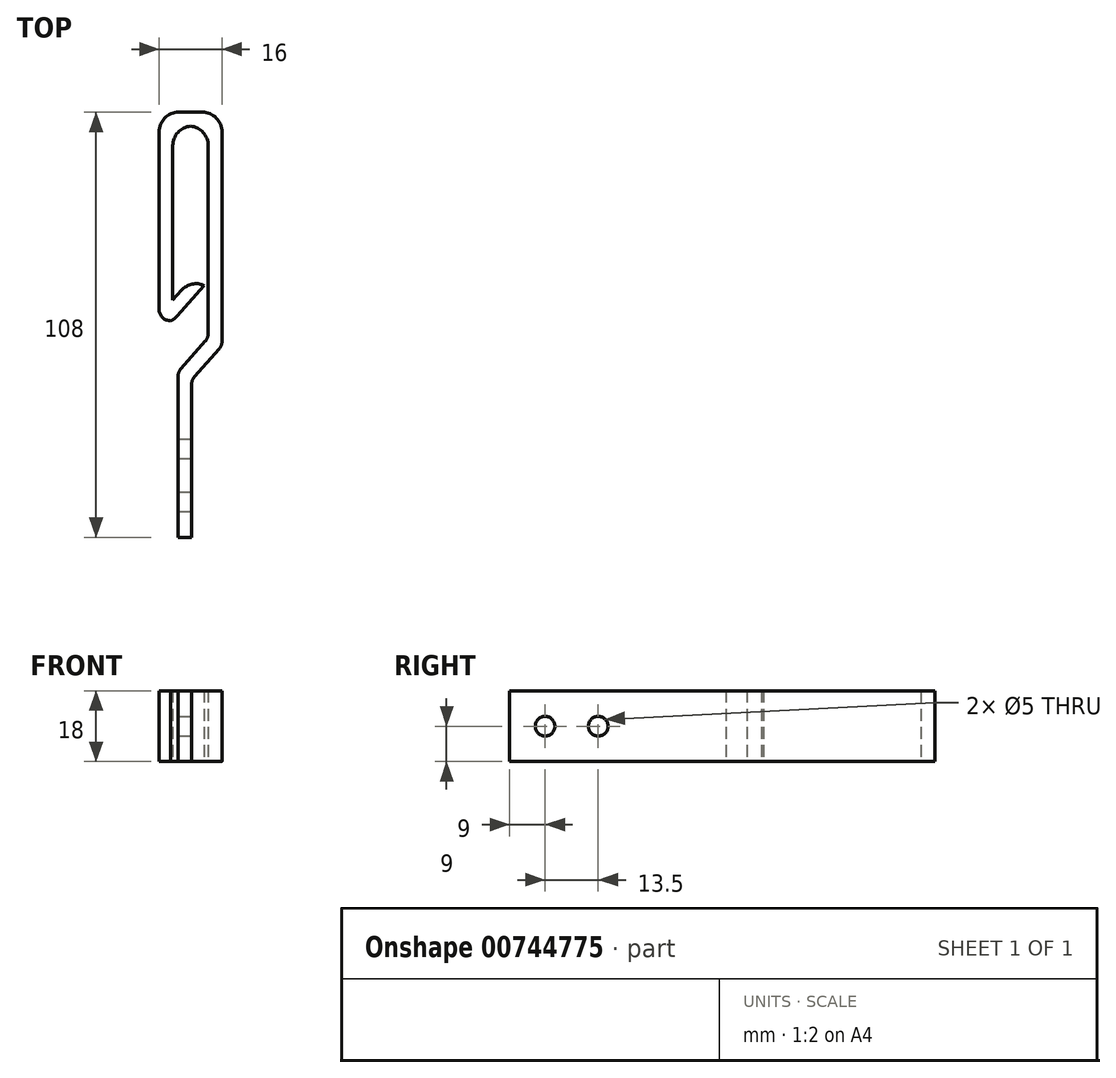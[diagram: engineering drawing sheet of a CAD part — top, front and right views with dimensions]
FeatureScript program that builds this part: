
annotation { "Feature Type Name" : "Feature", "Feature Type Description" : "" }
export const myFeature = defineFeature(function(context is Context, id is Id, definition is map)
    precondition{}
    {
        {
            var Q0;
            Q0=qCreatedBy(makeId("Top.planeOp"),FACE);
            var sketch = newSketch(context, id + "F0", { "sketchPlane" : qUnion([Q0])});
            skLineSegment(sketch, "E0.bottom", {"start": v(8, -54) * mm, "end": v(-8, -54) * mm});
            skLineSegment(sketch, "E0.top", {"start": v(8, 54) * mm, "end": v(-8, 54) * mm});
            skLineSegment(sketch, "E0.left", {"start": v(8, -54) * mm, "end": v(8, 54) * mm});
            skLineSegment(sketch, "E0.right", {"start": v(-8, -54) * mm, "end": v(-8, 54) * mm});
            skPoint(sketch, "E0.middle", {"position": v(0, 0) * mm});
            skLineSegment(sketch, "E1", {"start": v(4.5, 54) * mm, "end": v(4.5, -14) * mm});
            skLineSegment(sketch, "E2", {"start": v(-8, 50.5) * mm, "end": v(8, 50.5) * mm});
            skLineSegment(sketch, "E3", {"start": v(3.5, 54) * mm, "end": v(3.5, -14) * mm, "construction": true});
            skLineSegment(sketch, "E4.bottom", {"start": v(-8, 54) * mm, "end": v(-4.5, 54) * mm});
            skLineSegment(sketch, "E4.top", {"start": v(-8, 1) * mm, "end": v(-4.5, 1) * mm});
            skLineSegment(sketch, "E4.left", {"start": v(-8, 54) * mm, "end": v(-8, 1) * mm});
            skLineSegment(sketch, "E4.right", {"start": v(-4.5, 54) * mm, "end": v(-4.5, 1) * mm});
            skLineSegment(sketch, "E5", {"start": v(-4.5, 1) * mm, "end": v(3.5, 10) * mm});
            skLineSegment(sketch, "E6", {"start": v(3.5, 10) * mm, "end": v(0.88, 12.33) * mm});
            skLineSegment(sketch, "E7", {"start": v(0.88, 12.33) * mm, "end": v(-8, 2.33) * mm});
            skLineSegment(sketch, "E8", {"start": v(-8, -14) * mm, "end": v(8, -14) * mm, "construction": true});
            skLineSegment(sketch, "E9.bottom", {"start": v(-3.2, -54) * mm, "end": v(0.3, -54) * mm});
            skLineSegment(sketch, "E9.top", {"start": v(-3.2, -14) * mm, "end": v(0.3, -14) * mm});
            skLineSegment(sketch, "E9.left", {"start": v(-3.2, -54) * mm, "end": v(-3.2, -14) * mm});
            skLineSegment(sketch, "E9.right", {"start": v(0.3, -54) * mm, "end": v(0.3, -14) * mm});
            skLineSegment(sketch, "E10", {"start": v(0.3, -14) * mm, "end": v(8, -5.34) * mm});
            skLineSegment(sketch, "E11", {"start": v(-3.2, -14) * mm, "end": v(-3.2, -12) * mm});
            skLineSegment(sketch, "E12", {"start": v(-3.2, -12) * mm, "end": v(4.5, -3.34) * mm});
            skSolve(sketch);
        }
        {
            var Q0;
            {var subQ0=sQuery(id+"F0.wireOp",EDGE,"E0.right");var subQ1=sQuery(id+"F0.wireOp",EDGE,"E0.top");var subQ2=makeQuery(id+"F0.imprint","INTERSECT",VERTEX,{"derivedFrom":[subQ1,subQ0]});Q0=makeQuery(id+"F0.imprint","IMPRINT",FACE,{"disambiguationData":[TD([[makeQuery(id+"F0.imprint","IMPRINT",EDGE,{"disambiguationData":[TD([[subQ2,1.0]])],"derivedFrom":subQ1}),1.0]])]});}
            var Q1;
            {var subQ0=sQuery(id+"F0.wireOp",EDGE,"E1");var subQ1=sQuery(id+"F0.wireOp",EDGE,"E0.top");var subQ2=makeQuery(id+"F0.imprint","INTERSECT",VERTEX,{"derivedFrom":[subQ1,subQ0]});Q1=makeQuery(id+"F0.imprint","IMPRINT",FACE,{"disambiguationData":[TD([[makeQuery(id+"F0.imprint","IMPRINT",EDGE,{"disambiguationData":[TD([[subQ2,-1.0]])],"derivedFrom":subQ1}),1.0]])]});}
            var Q2;
            {var subQ0=sQuery(id+"F0.wireOp",EDGE,"E1");var subQ1=sQuery(id+"F0.wireOp",EDGE,"E0.top");var subQ2=makeQuery(id+"F0.imprint","INTERSECT",VERTEX,{"derivedFrom":[subQ1,subQ0]});Q2=makeQuery(id+"F0.imprint","IMPRINT",FACE,{"disambiguationData":[TD([[makeQuery(id+"F0.imprint","IMPRINT",EDGE,{"disambiguationData":[TD([[subQ2,1.0]])],"derivedFrom":subQ1}),1.0]])]});}
            var Q3;
            {var subQ3=sQuery(id+"F0.wireOp",EDGE,"E0.left");var subQ5=sQuery(id+"F0.wireOp",EDGE,"E10");var subQ6=makeQuery(id+"F0.imprint","INTERSECT",VERTEX,{"derivedFrom":[subQ3,subQ5]});Q3=makeQuery(id+"F0.imprint","IMPRINT",FACE,{"disambiguationData":[TD([[makeQuery(id+"F0.imprint","IMPRINT",EDGE,{"disambiguationData":[TD([[subQ6,-1.0]])],"derivedFrom":subQ3}),1.0]])]});}
            var Q4;
            {var subQ0=sQuery(id+"F0.wireOp",EDGE,"E7");var subQ1=sQuery(id+"F0.wireOp",EDGE,"E0.right");var subQ2=makeQuery(id+"F0.imprint","INTERSECT",VERTEX,{"derivedFrom":[subQ1,subQ0]});Q4=makeQuery(id+"F0.imprint","IMPRINT",FACE,{"disambiguationData":[TD([[makeQuery(id+"F0.imprint","IMPRINT",EDGE,{"disambiguationData":[TD([[subQ2,-1.0]])],"derivedFrom":subQ1}),-1.0]])]});}
            var Q5;
            {var subQ3=sQuery(id+"F0.wireOp",EDGE,"E4.top");Q5=makeQuery(id+"F0.imprint","IMPRINT",FACE,{"disambiguationData":[TD([[makeQuery(id+"F0.imprint","IMPRINT",EDGE,{"derivedFrom":subQ3}),1.0]])]});}
            var Q6;
            {var subQ0=sQuery(id+"F0.wireOp",EDGE,"E5");Q6=makeQuery(id+"F0.imprint","IMPRINT",FACE,{"disambiguationData":[TD([[makeQuery(id+"F0.imprint","IMPRINT",EDGE,{"derivedFrom":subQ0}),1.0]])]});}
            var Q7;
            {var subQ1=sQuery(id+"F0.wireOp",EDGE,"E9.top");Q7=makeQuery(id+"F0.imprint","IMPRINT",FACE,{"disambiguationData":[TD([[makeQuery(id+"F0.imprint","IMPRINT",EDGE,{"derivedFrom":subQ1}),1.0]])]});}
            var Q8;
            Q8=makeQuery(id+"F0.imprint","IMPRINT",FACE,{"disambiguationData":[TD([[makeQuery(id+"F0.imprint","IMPRINT",EDGE,{"derivedFrom":sQuery(id+"F0.wireOp",EDGE,"E9.top")}),-1.0]])]});
            extrude(context, id + "F1", {"entities" : qUnion([Q0, Q1, Q2, Q3, Q4, Q5, Q6, Q7, Q8]), "depth" : 18 * mm, "offsetDistance" : 25 * mm});
        }
        {
            var Q0;
            Q0=makeQuery(id+"F1.opExtrude","SWEPT_EDGE",EDGE,{"disambiguationData":[OSD([sQuery(id+"F0.wireOp",EDGE,"E0.left"),sQuery(id+"F0.wireOp",EDGE,"E10")])]});
            var Q1;
            Q1=makeQuery(id+"F1.opExtrude","SWEPT_EDGE",EDGE,{"disambiguationData":[OSD([sQuery(id+"F0.wireOp",EDGE,"E11"),sQuery(id+"F0.wireOp",EDGE,"E12")])]});
            var Q2;
            Q2=makeQuery(id+"F1.opExtrude","SWEPT_EDGE",EDGE,{"disambiguationData":[OSD([sQuery(id+"F0.wireOp",EDGE,"E1"),sQuery(id+"F0.wireOp",EDGE,"E12")])]});
            var Q3;
            Q3=makeQuery(id+"F1.opExtrude","SWEPT_EDGE",EDGE,{"disambiguationData":[OSD([sQuery(id+"F0.wireOp",EDGE,"E0.right"),sQuery(id+"F0.wireOp",EDGE,"E4.top")])]});
            var Q4;
            Q4=makeQuery(id+"F1.opExtrude","SWEPT_EDGE",EDGE,{"disambiguationData":[OSD([sQuery(id+"F0.wireOp",EDGE,"E9.top"),sQuery(id+"F0.wireOp",EDGE,"E9.right"),sQuery(id+"F0.wireOp",EDGE,"E10")])]});
            fillet(context, id + "F2", {"entities" : qUnion([Q0, Q1, Q2, Q3, Q4]), "radius" : 3 * mm, "tangentPropagation" : true, "allowEdgeOverflow" : false});
        }
        {
            var Q0;
            Q0=makeQuery(id+"F1.opExtrude","SWEPT_EDGE",EDGE,{"disambiguationData":[OSD([sQuery(id+"F0.wireOp",EDGE,"E2"),sQuery(id+"F0.wireOp",EDGE,"E4.right")])]});
            var Q1;
            Q1=makeQuery(id+"F1.opExtrude","SWEPT_EDGE",EDGE,{"disambiguationData":[OSD([sQuery(id+"F0.wireOp",EDGE,"E1"),sQuery(id+"F0.wireOp",EDGE,"E2")])]});
            var Q2;
            Q2=makeQuery(id+"F1.opExtrude","SWEPT_EDGE",EDGE,{"disambiguationData":[OSD([sQuery(id+"F0.wireOp",EDGE,"E0.top"),sQuery(id+"F0.wireOp",EDGE,"E0.left")])]});
            var Q3;
            Q3=makeQuery(id+"F1.opExtrude","SWEPT_EDGE",EDGE,{"disambiguationData":[OSD([sQuery(id+"F0.wireOp",EDGE,"E0.top"),sQuery(id+"F0.wireOp",EDGE,"E0.right")])]});
            var Q4;
            Q4=makeQuery(id+"F1.opExtrude","SWEPT_EDGE",EDGE,{"disambiguationData":[OSD([sQuery(id+"F0.wireOp",EDGE,"E4.top"),sQuery(id+"F0.wireOp",EDGE,"E4.right"),sQuery(id+"F0.wireOp",EDGE,"E5")])]});
            var Q5;
            Q5=makeQuery(id+"F1.opExtrude","SWEPT_EDGE",EDGE,{"disambiguationData":[OSD([sQuery(id+"F0.wireOp",EDGE,"E6"),sQuery(id+"F0.wireOp",EDGE,"E7")])]});
            fillet(context, id + "F3", {"entities" : qUnion([Q0, Q1, Q2, Q3, Q4, Q5]), "radius" : 5 * mm, "tangentPropagation" : true, "allowEdgeOverflow" : false});
        }
        {
            var Q0;
            Q0=makeQuery(id+"F1.opExtrude","SWEPT_FACE",FACE,{"disambiguationData":[OSD([sQuery(id+"F0.wireOp",EDGE,"E9.right")])]});
            var sketch = newSketch(context, id + "F4", { "sketchPlane" : qUnion([Q0])});
            skLineSegment(sketch, "E13", {"start": v(-54, 9) * mm, "end": v(-15.14, 9) * mm, "construction": true});
            skCircle(sketch, "E14", {"center": v(-45, 9) * mm, "radius": 2.5 * mm});
            skCircle(sketch, "E15", {"center": v(-31.5, 9) * mm, "radius": 2.5 * mm});
            skSolve(sketch);
        }
        {
            var Q0;
            Q0=makeQuery(id+"F4.imprint","IMPRINT",FACE,{"disambiguationData":[TD([[makeQuery(id+"F4.imprint","IMPRINT",EDGE,{"derivedFrom":sQuery(id+"F4.wireOp",EDGE,"E14")}),1.0]])]});
            var Q1;
            Q1=makeQuery(id+"F4.imprint","IMPRINT",FACE,{"disambiguationData":[TD([[makeQuery(id+"F4.imprint","IMPRINT",EDGE,{"derivedFrom":sQuery(id+"F4.wireOp",EDGE,"E15")}),1.0]])]});
            extrude(context, id + "F5", {"entities" : qUnion([Q0, Q1]), "operationType" : NewBodyOperationType.REMOVE, "endBound" : BoundingType.UP_TO_NEXT, "oppositeDirection" : true, "depth" : 25 * mm, "offsetDistance" : 25 * mm});
        }
    });
